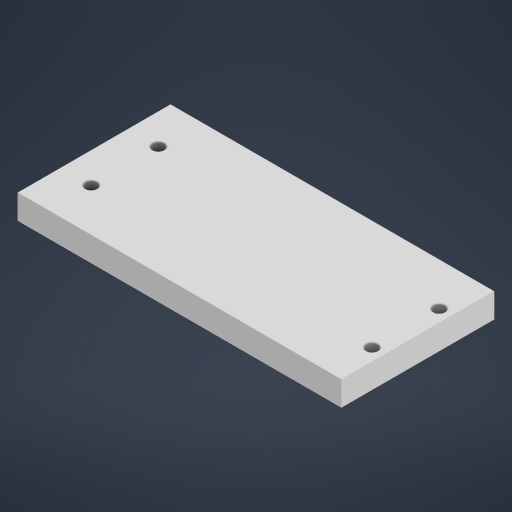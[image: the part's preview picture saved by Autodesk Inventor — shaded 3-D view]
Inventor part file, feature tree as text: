
AUTODESK INVENTOR PART (.ipt)
format: ipt  version: 2023.2 (Build 272271000, 271)  size: 202,752 bytes
history: native  units: mm
features: sketch x1
ambient origin geometry x8: Origin, YZ Plane, XZ Plane, XY Plane, X Axis, Y Axis, Z Axis, Center Point
bodies: Body1 (feature_tree)
feature tree (1):
  sketch  "Sketch1"  dims[d228=25.0mm d229=53.0mm d232=11.0mm d233=5.0mm d234=2.0mm d238=4.0mm d239=0.0mm d240=2.0mm d9=0.5mm d10=0.872665mm d11=0.5mm d12=0.872665mm d13=0.5mm d14=0.872665mm d27=0.5mm d28=0.872665mm d29=0.5mm d30=0.872665mm d88=0.5mm d89=0.872665mm d90=0.5mm d91=0.872665mm d116=0.5mm d117=0.872665mm d118=0.5mm d119=0.872665mm d154=0.5mm d155=0.872665mm d156=0.5mm d157=0.872665mm d181=0.5mm d182=0.872665mm d183=0.5mm d184=0.872665mm d221=0.5mm d222=0.872665mm d223=0.5mm d224=0.872665mm]
